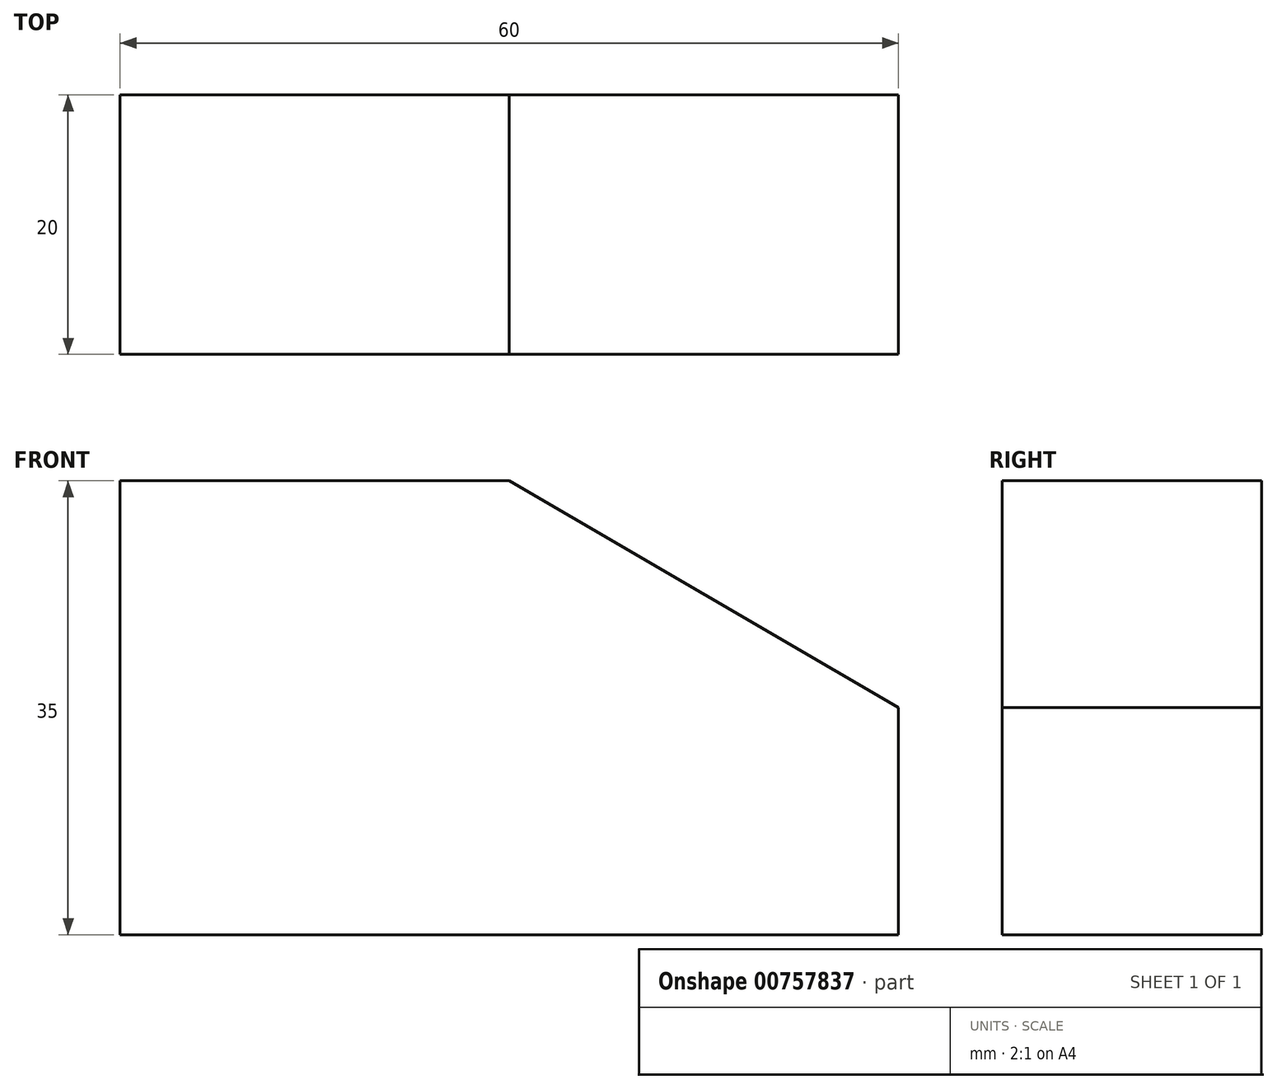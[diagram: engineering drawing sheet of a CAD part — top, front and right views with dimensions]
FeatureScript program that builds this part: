
annotation { "Feature Type Name" : "Feature", "Feature Type Description" : "" }
export const myFeature = defineFeature(function(context is Context, id is Id, definition is map)
    precondition{}
    {
        {
            var Q0;
            Q0=qCreatedBy(makeId("Front.planeOp"),FACE);
            var sketch = newSketch(context, id + "F0", { "sketchPlane" : qUnion([Q0])});
            skLineSegment(sketch, "E0.bottom", {"start": v(0, 0) * mm, "end": v(60, 0) * mm});
            skLineSegment(sketch, "E0.top", {"start": v(0, 35) * mm, "end": v(60, 35) * mm});
            skLineSegment(sketch, "E0.left", {"start": v(0, 0) * mm, "end": v(0, 35) * mm});
            skLineSegment(sketch, "E0.right", {"start": v(60, 0) * mm, "end": v(60, 35) * mm});
            skSolve(sketch);
        }
        {
            var Q0;
            {var subQ3=sQuery(id+"F0.wireOp",EDGE,"rwG7CODo-Gvo8-TEka-HWyY-ZXxTwNUBx80L");Q0=makeQuery(id+"F0.imprint","IMPRINT",FACE,{"disambiguationData":[TD([[makeQuery(id+"F0.imprint","IMPRINT",EDGE,{"derivedFrom":subQ3}),1.0]])]});}
            var Q1;
            {var subQ1=sQuery(id+"F0.wireOp",EDGE,"E0.bottom");Q1=makeQuery(id+"F0.imprint","IMPRINT",FACE,{"disambiguationData":[TD([[makeQuery(id+"F0.imprint","IMPRINT",EDGE,{"derivedFrom":subQ1}),1.0]])]});}
            extrude(context, id + "F1", {"entities" : qUnion([Q0, Q1]), "depth" : 20 * mm, "offsetDistance" : 25 * mm});
        }
        {
            var Q0;
            Q0=makeQuery(id+"F1.opExtrude","CAP_FACE",FACE,{"disambiguationData":[OSD([sQuery(id+"F0.wireOp",EDGE,"E0.bottom"),sQuery(id+"F0.wireOp",EDGE,"E0.top"),sQuery(id+"F0.wireOp",EDGE,"E0.left"),sQuery(id+"F0.wireOp",EDGE,"E0.right")])],"isStart":false});
            var sketch = newSketch(context, id + "F2", { "sketchPlane" : qUnion([Q0])});
            skLineSegment(sketch, "E1", {"start": v(30, 35) * mm, "end": v(60, 17.5) * mm});
            skSolve(sketch);
        }
        {
            var Q0;
            Q0 = qSketchRegion(id + "F2", true);
            var Q1;
            {var subQ0=sQuery(id+"F2.wireOp",EDGE,"E1");Q1=makeQuery(id+"F2.imprint","IMPRINT",FACE,{"disambiguationData":[TD([[makeQuery(id+"F2.imprint","IMPRINT",EDGE,{"derivedFrom":subQ0}),1.0]])]});}
            extrude(context, id + "F3", {"entities" : qUnion([Q0, Q1]), "operationType" : NewBodyOperationType.REMOVE, "oppositeDirection" : true, "depth" : 25 * mm, "offsetDistance" : 25 * mm});
        }
    });
